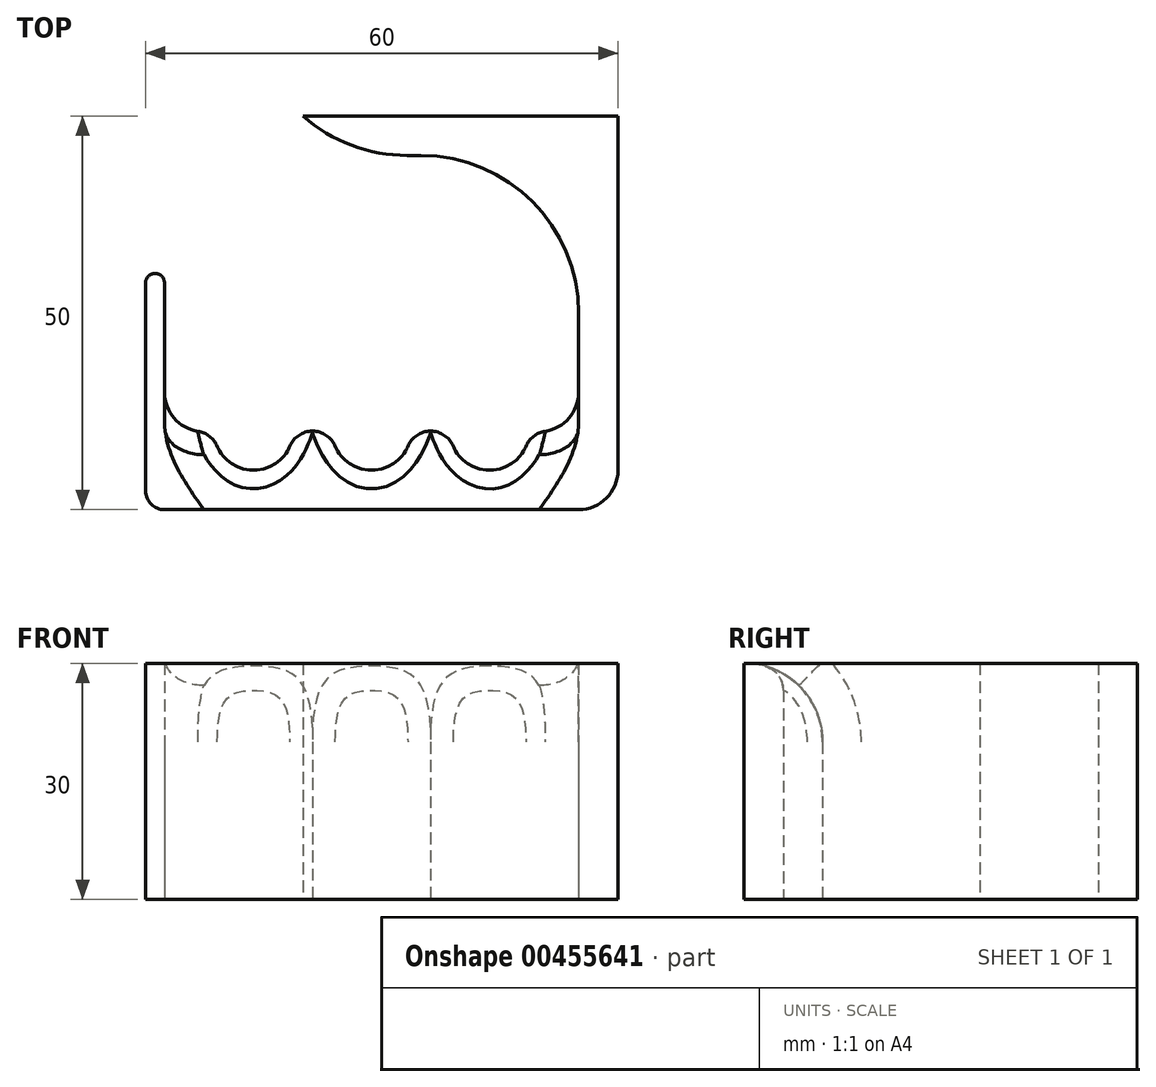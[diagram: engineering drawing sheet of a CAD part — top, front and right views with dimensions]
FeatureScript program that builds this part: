
annotation { "Feature Type Name" : "Feature", "Feature Type Description" : "" }
export const myFeature = defineFeature(function(context is Context, id is Id, definition is map)
    precondition{}
    {
        {
            var Q0;
            Q0=qCreatedBy(makeId("Top.planeOp"),FACE);
            var sketch = newSketch(context, id + "F0", { "sketchPlane" : qUnion([Q0])});
            skLineSegment(sketch, "E0", {"start": v(-26.52, 0) * mm, "end": v(33.48, 0) * mm});
            skLineSegment(sketch, "E1", {"start": v(33.48, 0) * mm, "end": v(33.48, 50) * mm});
            skLineSegment(sketch, "E2", {"start": v(33.48, 50) * mm, "end": v(-6.52, 50) * mm});
            skLineSegment(sketch, "E3", {"start": v(-6.52, 50) * mm, "end": v(-6.52, 45) * mm});
            skLineSegment(sketch, "E4", {"start": v(-6.52, 45) * mm, "end": v(28.48, 45) * mm});
            skLineSegment(sketch, "E5", {"start": v(28.48, 45) * mm, "end": v(28.48, 10) * mm});
            skLineSegment(sketch, "E6", {"start": v(28.48, 10) * mm, "end": v(-24.12, 10) * mm});
            skLineSegment(sketch, "E7", {"start": v(-24.12, 10) * mm, "end": v(-24.12, 30) * mm});
            skLineSegment(sketch, "E8", {"start": v(-24.12, 30) * mm, "end": v(-26.52, 30) * mm});
            skLineSegment(sketch, "E9", {"start": v(-26.52, 30) * mm, "end": v(-26.52, 0) * mm});
            skSolve(sketch);
        }
        {
            var Q0;
            Q0 = qSketchRegion(id + "F0", true);
            extrude(context, id + "F1", {"entities" : qUnion([Q0]), "depth" : 30 * mm});
        }
        {
            var Q0;
            Q0=makeQuery(id+"F1.opExtrude","CAP_EDGE",EDGE,{"disambiguationData":[OSD([sQuery(id+"F0.wireOp",EDGE,"E6")])],"isStart":false});
            fillet(context, id + "F2", {"entities" : qUnion([Q0]), "radius" : 10 * mm, "tangentPropagation" : true, "allowEdgeOverflow" : false});
        }
        {
            var Q0;
            Q0=makeQuery(id+"F1.opExtrude","SWEPT_EDGE",EDGE,{"disambiguationData":[OSD([sQuery(id+"F0.wireOp",EDGE,"E3"),sQuery(id+"F0.wireOp",EDGE,"E4")])]});
            var Q1;
            Q1=makeQuery(id+"F1.opExtrude","SWEPT_EDGE",EDGE,{"disambiguationData":[OSD([sQuery(id+"F0.wireOp",EDGE,"E4"),sQuery(id+"F0.wireOp",EDGE,"E5")])]});
            fillet(context, id + "F3", {"entities" : qUnion([Q0, Q1]), "radius" : 20 * mm, "tangentPropagation" : true, "allowEdgeOverflow" : false});
        }
        {
            var Q0;
            Q0=makeQuery(id+"F1.opExtrude","SWEPT_EDGE",EDGE,{"disambiguationData":[OSD([sQuery(id+"F0.wireOp",EDGE,"E8"),sQuery(id+"F0.wireOp",EDGE,"E9")])]});
            var Q1;
            Q1=makeQuery(id+"F1.opExtrude","SWEPT_EDGE",EDGE,{"disambiguationData":[OSD([sQuery(id+"F0.wireOp",EDGE,"E7"),sQuery(id+"F0.wireOp",EDGE,"E8")])]});
            fillet(context, id + "F4", {"entities" : qUnion([Q0, Q1]), "radius" : 1.2 * mm, "tangentPropagation" : true, "allowEdgeOverflow" : false});
        }
        {
            var Q0;
            Q0=makeQuery(id+"F1.opExtrude","SWEPT_EDGE",EDGE,{"disambiguationData":[OSD([sQuery(id+"F0.wireOp",EDGE,"E0"),sQuery(id+"F0.wireOp",EDGE,"E9")])]});
            fillet(context, id + "F5", {"entities" : qUnion([Q0]), "radius" : 2.4 * mm, "tangentPropagation" : true, "allowEdgeOverflow" : false});
        }
        {
            var Q0;
            Q0=makeQuery(id+"F1.opExtrude","SWEPT_EDGE",EDGE,{"disambiguationData":[OSD([sQuery(id+"F0.wireOp",EDGE,"E0"),sQuery(id+"F0.wireOp",EDGE,"E1")])]});
            fillet(context, id + "F6", {"entities" : qUnion([Q0]), "radius" : 5 * mm, "tangentPropagation" : true, "allowEdgeOverflow" : false});
        }
        {
            var Q0;
            Q0=qCreatedBy(makeId("Top.planeOp"),FACE);
            var sketch = newSketch(context, id + "F7", { "sketchPlane" : qUnion([Q0])});
            skCircle(sketch, "E10", {"center": v(-12.82, 10) * mm, "radius": 5 * mm});
            skCircle(sketch, "E11", {"center": v(2.18, 10) * mm, "radius": 5 * mm});
            skCircle(sketch, "E12", {"center": v(17.18, 10) * mm, "radius": 5 * mm});
            skSolve(sketch);
        }
        {
            var Q0;
            Q0 = qSketchRegion(id + "F7", true);
            extrude(context, id + "F8", {"entities" : qUnion([Q0]), "operationType" : NewBodyOperationType.REMOVE, "depth" : 30 * mm});
        }
        {
            var Q0;
            Q0=makeQuery(id+"F8.boolean.opBoolean","INTERSECT",EDGE,{"derivedFrom":[makeQuery(id+"F2.opFillet","BLEND_FACE",FACE,{"disambiguationData":[OSD([sQuery(id+"F0.wireOp",EDGE,"E6")])]}),makeQuery(id+"F8.opExtrude","SWEPT_FACE",FACE,{"disambiguationData":[OSD([sQuery(id+"F7.wireOp",EDGE,"E10")])]})]});
            var Q1;
            Q1=makeQuery(id+"F8.boolean.opBoolean","INTERSECT",EDGE,{"derivedFrom":[makeQuery(id+"F2.opFillet","BLEND_FACE",FACE,{"disambiguationData":[OSD([sQuery(id+"F0.wireOp",EDGE,"E6")])]}),makeQuery(id+"F8.opExtrude","SWEPT_FACE",FACE,{"disambiguationData":[OSD([sQuery(id+"F7.wireOp",EDGE,"E11")])]})]});
            var Q2;
            Q2=makeQuery(id+"F8.boolean.opBoolean","INTERSECT",EDGE,{"derivedFrom":[makeQuery(id+"F2.opFillet","BLEND_FACE",FACE,{"disambiguationData":[OSD([sQuery(id+"F0.wireOp",EDGE,"E6")])]}),makeQuery(id+"F8.opExtrude","SWEPT_FACE",FACE,{"disambiguationData":[OSD([sQuery(id+"F7.wireOp",EDGE,"E12")])]})]});
            fillet(context, id + "F9", {"entities" : qUnion([Q0, Q1, Q2]), "radius" : 3.2 * mm, "tangentPropagation" : true, "allowEdgeOverflow" : false});
        }
        {
            var Q0;
            Q0=makeQuery(id+"F1.opExtrude","SWEPT_EDGE",EDGE,{"disambiguationData":[OSD([sQuery(id+"F0.wireOp",EDGE,"E5"),sQuery(id+"F0.wireOp",EDGE,"E6")])]});
            var Q1;
            Q1=makeQuery(id+"F1.opExtrude","SWEPT_EDGE",EDGE,{"disambiguationData":[OSD([sQuery(id+"F0.wireOp",EDGE,"E6"),sQuery(id+"F0.wireOp",EDGE,"E7")])]});
            fillet(context, id + "F10", {"entities" : qUnion([Q0, Q1]), "radius" : 5 * mm, "tangentPropagation" : true, "allowEdgeOverflow" : false});
        }
    });
